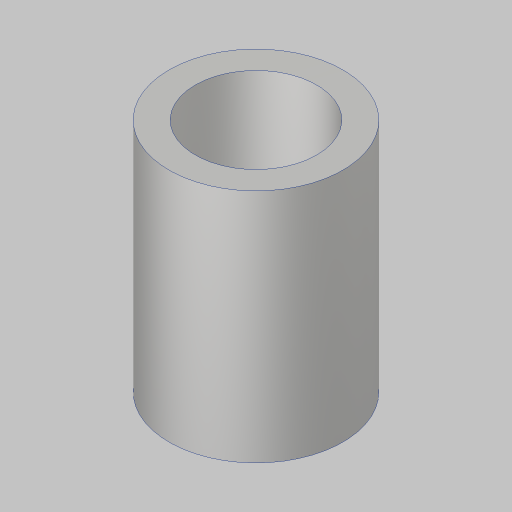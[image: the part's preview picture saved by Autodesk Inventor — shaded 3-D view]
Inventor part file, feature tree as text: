
AUTODESK INVENTOR PART (.ipt)
format: ipt  version: 2023.5 (Build 275446000, 446)  size: 109,056 bytes
history: native  units: in
note: dims shown in document units (in); Inventor stores cm internally (conversion verified against a paired STEP export)
features: extrude x1, sketch x1
ambient origin geometry x8: Origin, YZ Plane, XZ Plane, XY Plane, X Axis, Y Axis, Z Axis, Center Point
bodies: Solid1 (feature_tree)
feature tree (2):
  extrude  "Extrusion1"  Depth=1.125in
  sketch  "Sketch1"  dims[d0=0.58in d1=0.125in d2=1.125in d3=0.0in]
